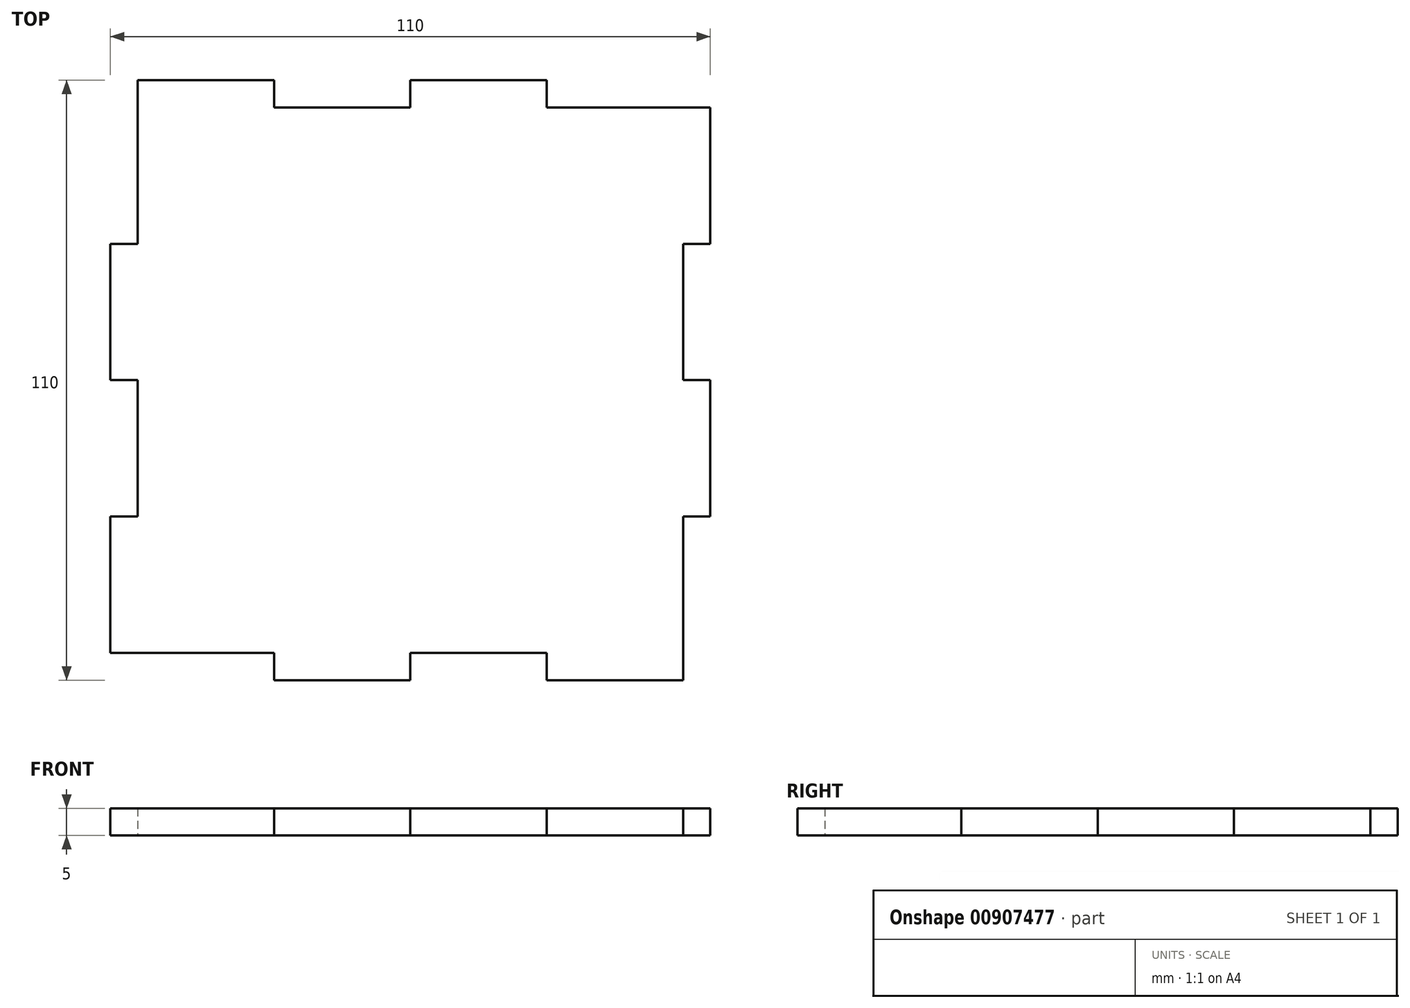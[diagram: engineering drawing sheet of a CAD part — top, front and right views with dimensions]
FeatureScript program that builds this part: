
annotation { "Feature Type Name" : "Feature", "Feature Type Description" : "" }
export const myFeature = defineFeature(function(context is Context, id is Id, definition is map)
    precondition{}
    {
        {
            var Q0;
            Q0=qCreatedBy(makeId("Top.planeOp"),FACE);
            var sketch = newSketch(context, id + "F0", { "sketchPlane" : qUnion([Q0])});
            skLineSegment(sketch, "E0.bottom", {"start": v(-25, 50) * mm, "end": v(0, 50) * mm});
            skLineSegment(sketch, "E1", {"start": v(-50, 50) * mm, "end": v(-50, 55) * mm});
            skLineSegment(sketch, "E2", {"start": v(-50, 55) * mm, "end": v(-25, 55) * mm});
            skLineSegment(sketch, "E3", {"start": v(-25, 55) * mm, "end": v(-25, 50) * mm});
            skLineSegment(sketch, "E4", {"start": v(0, 50) * mm, "end": v(0, 55) * mm});
            skLineSegment(sketch, "E5", {"start": v(0, 55) * mm, "end": v(25, 55) * mm});
            skLineSegment(sketch, "E6", {"start": v(25, 55) * mm, "end": v(25, 50) * mm});
            skPoint(sketch, "E0.top.end.orphan", {"position": v(50, -50) * mm});
            skLineSegment(sketch, "E7.trimOffspring", {"start": v(25, 50) * mm, "end": v(50, 50) * mm});
            skLineSegment(sketch, "E8.1.0", {"start": v(-50, -50) * mm, "end": v(-55, -50) * mm});
            skLineSegment(sketch, "E8.1.1", {"start": v(-55, -50) * mm, "end": v(-55, -25) * mm});
            skLineSegment(sketch, "E8.1.2", {"start": v(-55, -25) * mm, "end": v(-50, -25) * mm});
            skLineSegment(sketch, "E8.1.3", {"start": v(-50, -25) * mm, "end": v(-50, 0) * mm});
            skLineSegment(sketch, "E8.1.4", {"start": v(-50, 0) * mm, "end": v(-55, 0) * mm});
            skLineSegment(sketch, "E8.1.5", {"start": v(-55, 0) * mm, "end": v(-55, 25) * mm});
            skLineSegment(sketch, "E8.1.6", {"start": v(-55, 25) * mm, "end": v(-50, 25) * mm});
            skLineSegment(sketch, "E8.1.7", {"start": v(-50, 25) * mm, "end": v(-50, 50) * mm});
            skLineSegment(sketch, "E8.2.0", {"start": v(50, -50) * mm, "end": v(50, -55) * mm});
            skLineSegment(sketch, "E8.2.1", {"start": v(50, -55) * mm, "end": v(25, -55) * mm});
            skLineSegment(sketch, "E8.2.2", {"start": v(25, -55) * mm, "end": v(25, -50) * mm});
            skLineSegment(sketch, "E8.2.3", {"start": v(25, -50) * mm, "end": v(0, -50) * mm});
            skLineSegment(sketch, "E8.2.4", {"start": v(0, -50) * mm, "end": v(0, -55) * mm});
            skLineSegment(sketch, "E8.2.5", {"start": v(0, -55) * mm, "end": v(-25, -55) * mm});
            skLineSegment(sketch, "E8.2.6", {"start": v(-25, -55) * mm, "end": v(-25, -50) * mm});
            skLineSegment(sketch, "E8.2.7", {"start": v(-25, -50) * mm, "end": v(-50, -50) * mm});
            skLineSegment(sketch, "E8.3.0", {"start": v(50, 50) * mm, "end": v(55, 50) * mm});
            skLineSegment(sketch, "E8.3.1", {"start": v(55, 50) * mm, "end": v(55, 25) * mm});
            skLineSegment(sketch, "E8.3.2", {"start": v(55, 25) * mm, "end": v(50, 25) * mm});
            skLineSegment(sketch, "E8.3.3", {"start": v(50, 25) * mm, "end": v(50, 0) * mm});
            skLineSegment(sketch, "E8.3.4", {"start": v(50, 0) * mm, "end": v(55, 0) * mm});
            skLineSegment(sketch, "E8.3.5", {"start": v(55, 0) * mm, "end": v(55, -25) * mm});
            skLineSegment(sketch, "E8.3.6", {"start": v(55, -25) * mm, "end": v(50, -25) * mm});
            skLineSegment(sketch, "E8.3.7", {"start": v(50, -25) * mm, "end": v(50, -50) * mm});
            skPoint(sketch, "E8.center", {"position": v(0, 0) * mm});
            skSolve(sketch);
        }
        {
            var Q0;
            Q0=makeQuery(id+"F0.imprint","IMPRINT",FACE,{"disambiguationData":[TD([[makeQuery(id+"F0.imprint","IMPRINT",EDGE,{"derivedFrom":sQuery(id+"F0.wireOp",EDGE,"E1")}),-1.0]])]});
            extrude(context, id + "F1", {"entities" : qUnion([Q0]), "depth" : 5 * mm, "offsetDistance" : 25 * mm});
        }
    });
